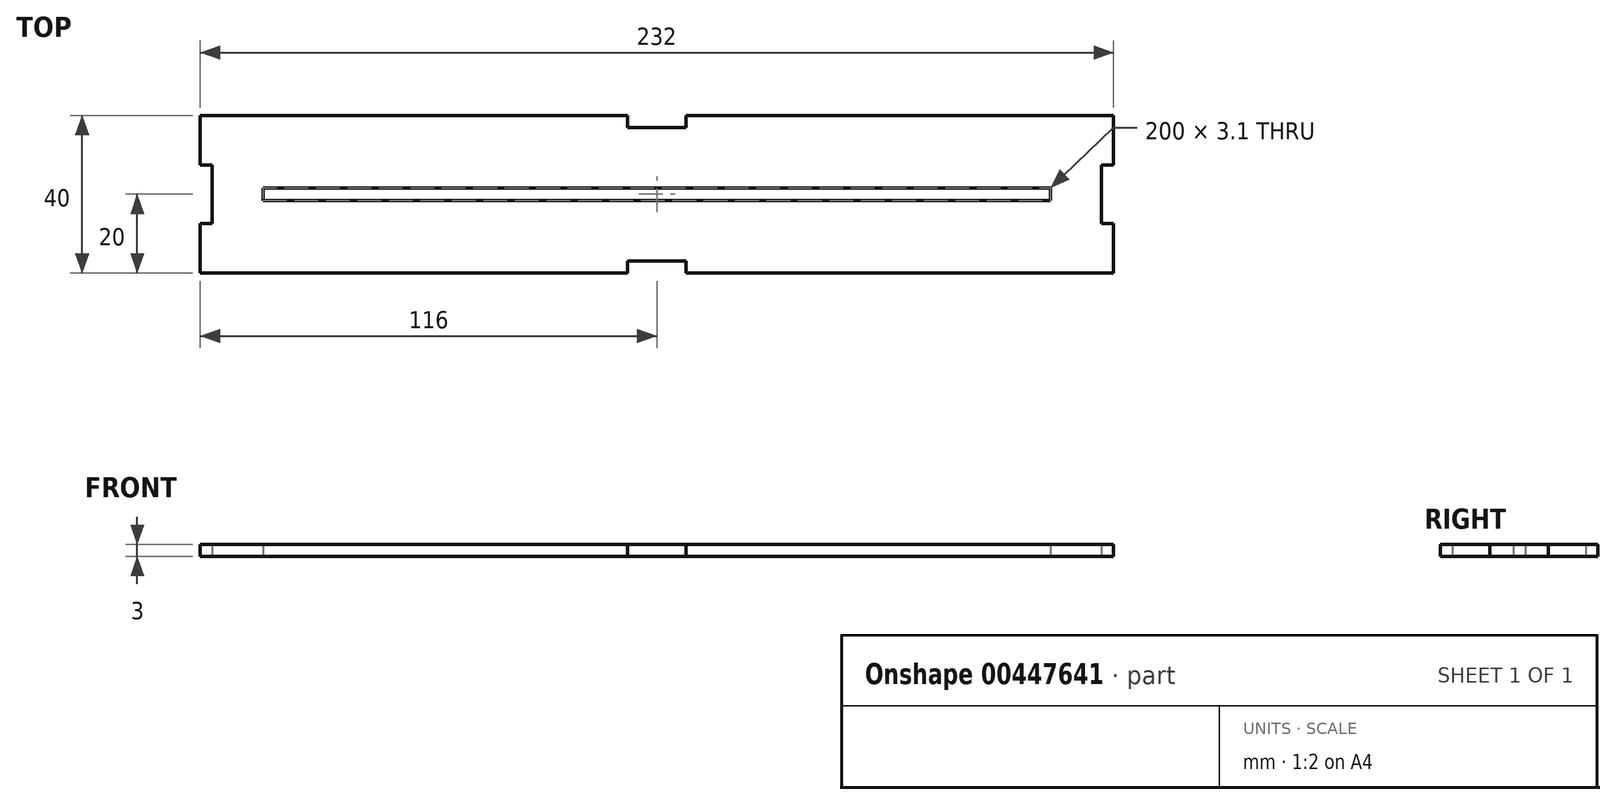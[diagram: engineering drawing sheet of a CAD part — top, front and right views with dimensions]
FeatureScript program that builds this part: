
annotation { "Feature Type Name" : "Feature", "Feature Type Description" : "" }
export const myFeature = defineFeature(function(context is Context, id is Id, definition is map)
    precondition{}
    {
        {
            var Q0;
            Q0=qCreatedBy(makeId("Top.planeOp"),FACE);
            var sketch = newSketch(context, id + "F0", { "sketchPlane" : qUnion([Q0])});
            skLineSegment(sketch, "E0.bottom", {"start": v(116, -20) * mm, "end": v(-116, -20) * mm});
            skLineSegment(sketch, "E0.top", {"start": v(116, 20) * mm, "end": v(-116, 20) * mm});
            skLineSegment(sketch, "E0.left", {"start": v(116, -20) * mm, "end": v(116, 20) * mm});
            skLineSegment(sketch, "E0.right", {"start": v(-116, -20) * mm, "end": v(-116, 20) * mm});
            skPoint(sketch, "E0.middle", {"position": v(0, 0) * mm});
            skLineSegment(sketch, "E1.bottom", {"start": v(-116, -7.45) * mm, "end": v(-112.95, -7.45) * mm});
            skLineSegment(sketch, "E1.top", {"start": v(-116, 7.45) * mm, "end": v(-112.95, 7.45) * mm});
            skLineSegment(sketch, "E1.left", {"start": v(-116, -7.45) * mm, "end": v(-116, 7.45) * mm});
            skLineSegment(sketch, "E1.right", {"start": v(-112.95, -7.45) * mm, "end": v(-112.95, 7.45) * mm});
            skPoint(sketch, "E1.middle", {"position": v(-114.47, 0) * mm});
            skLineSegment(sketch, "E2.bottom", {"start": v(116, -7.45) * mm, "end": v(112.95, -7.45) * mm});
            skLineSegment(sketch, "E2.top", {"start": v(116, 7.45) * mm, "end": v(112.95, 7.45) * mm});
            skLineSegment(sketch, "E2.left", {"start": v(116, -7.45) * mm, "end": v(116, 7.45) * mm});
            skLineSegment(sketch, "E2.right", {"start": v(112.95, -7.45) * mm, "end": v(112.95, 7.45) * mm});
            skPoint(sketch, "E2.middle", {"position": v(114.47, 0) * mm});
            skLineSegment(sketch, "E3.bottom", {"start": v(100, -1.55) * mm, "end": v(-100, -1.55) * mm});
            skLineSegment(sketch, "E3.top", {"start": v(100, 1.55) * mm, "end": v(-100, 1.55) * mm});
            skLineSegment(sketch, "E3.left", {"start": v(100, -1.55) * mm, "end": v(100, 1.55) * mm});
            skLineSegment(sketch, "E3.right", {"start": v(-100, -1.55) * mm, "end": v(-100, 1.55) * mm});
            skLineSegment(sketch, "E4.bottom", {"start": v(7.45, 16.95) * mm, "end": v(-7.45, 16.95) * mm});
            skLineSegment(sketch, "E4.top", {"start": v(7.45, 20) * mm, "end": v(-7.45, 20) * mm});
            skLineSegment(sketch, "E4.left", {"start": v(7.45, 16.95) * mm, "end": v(7.45, 20) * mm});
            skLineSegment(sketch, "E4.right", {"start": v(-7.45, 16.95) * mm, "end": v(-7.45, 20) * mm});
            skPoint(sketch, "E4.middle", {"position": v(0, 18.47) * mm});
            skLineSegment(sketch, "E5.bottom", {"start": v(7.45, -20) * mm, "end": v(-7.45, -20) * mm});
            skLineSegment(sketch, "E5.top", {"start": v(7.45, -16.95) * mm, "end": v(-7.45, -16.95) * mm});
            skLineSegment(sketch, "E5.left", {"start": v(7.45, -20) * mm, "end": v(7.45, -16.95) * mm});
            skLineSegment(sketch, "E5.right", {"start": v(-7.45, -20) * mm, "end": v(-7.45, -16.95) * mm});
            skPoint(sketch, "E5.middle", {"position": v(0, -18.48) * mm});
            skSolve(sketch);
        }
        {
            var Q0;
            {var subQ3=sQuery(id+"F0.wireOp",EDGE,"E0.top");Q0=makeQuery(id+"F0.imprint","IMPRINT",FACE,{"disambiguationData":[TD([[makeQuery(id+"F0.imprint","IMPRINT",EDGE,{"derivedFrom":subQ3}),1.0]])]});}
            extrude(context, id + "F1", {"entities" : qUnion([Q0]), "depth" : 3 * mm});
        }
    });
